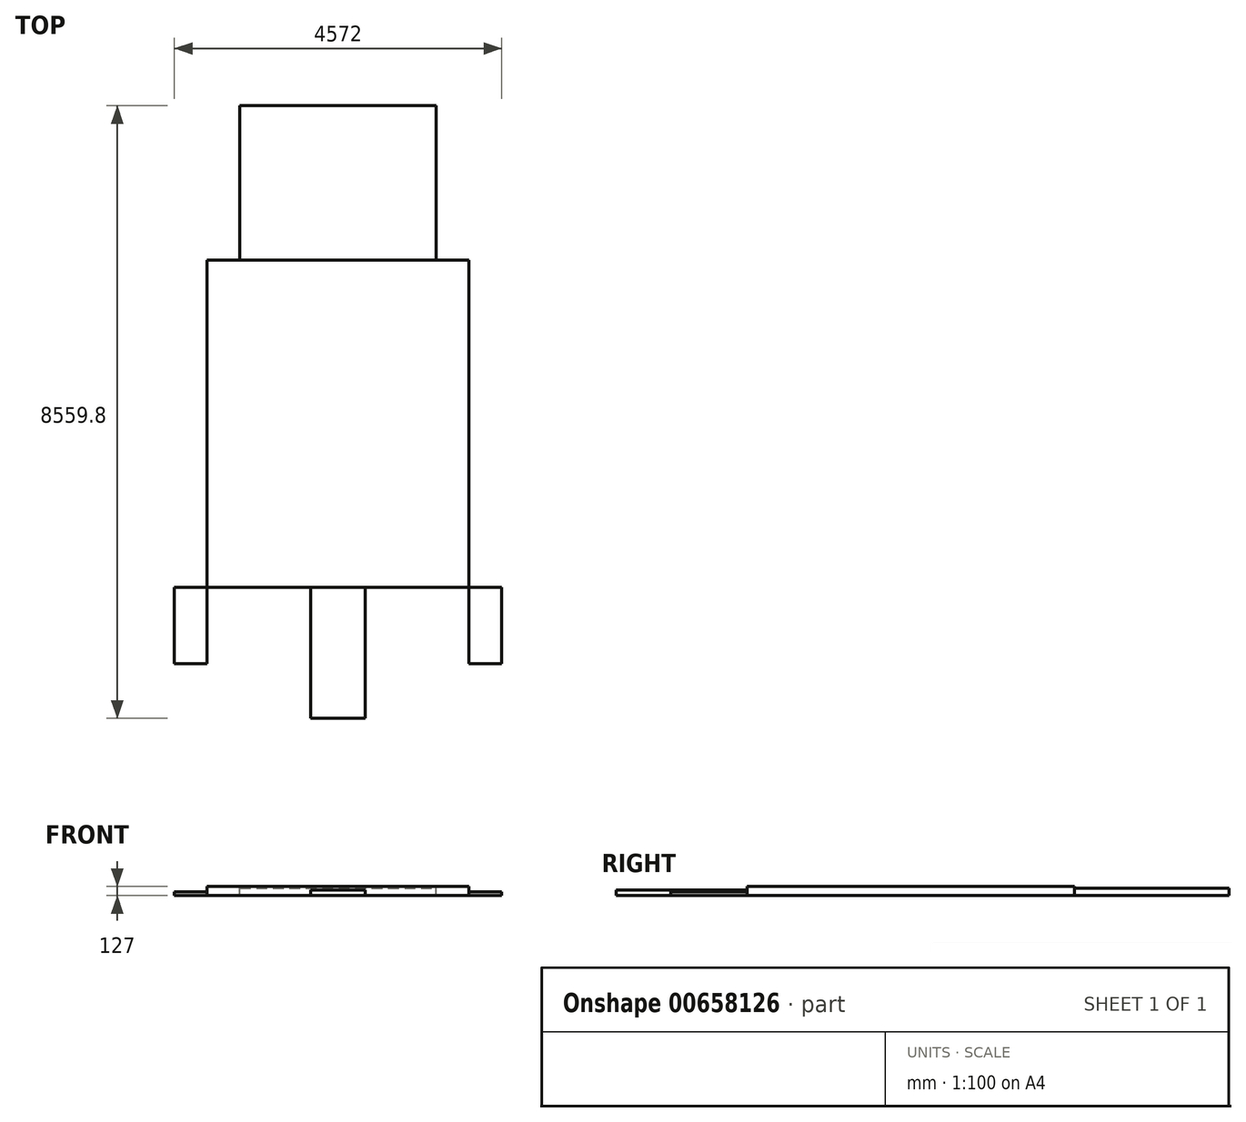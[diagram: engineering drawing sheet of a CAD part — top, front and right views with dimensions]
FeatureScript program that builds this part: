
annotation { "Feature Type Name" : "Feature", "Feature Type Description" : "" }
export const myFeature = defineFeature(function(context is Context, id is Id, definition is map)
    precondition{}
    {
        {
            var Q0;
            Q0=qCreatedBy(makeId("Top.planeOp"),FACE);
            var sketch = newSketch(context, id + "F0", { "sketchPlane" : qUnion([Q0])});
            skLineSegment(sketch, "E0.top", {"start": v(0, 4572) * mm, "end": v(3657.6, 4572) * mm});
            skLineSegment(sketch, "E0.left", {"start": v(0, 0) * mm, "end": v(0, 4572) * mm});
            skLineSegment(sketch, "E0.right", {"start": v(3657.6, 0) * mm, "end": v(3657.6, 4572) * mm});
            skLineSegment(sketch, "E1", {"start": v(0, 0) * mm, "end": v(3657.6, 0) * mm});
            skSolve(sketch);
        }
        {
            var Q0;
            Q0=makeQuery(id+"F0.imprint","IMPRINT",FACE,{"disambiguationData":[TD([[makeQuery(id+"F0.imprint","IMPRINT",EDGE,{"derivedFrom":sQuery(id+"F0.wireOp",EDGE,"E0.top")}),-1.0]])]});
            extrude(context, id + "F1", {"entities" : qUnion([Q0]), "depth" : 127 * mm, "offsetDistance" : 25.4 * mm});
        }
        {
            var Q0;
            Q0=makeQuery(id+"F1.opExtrude","CAP_FACE",FACE,{"disambiguationData":[OSD([sQuery(id+"F0.wireOp",EDGE,"E0.top"),sQuery(id+"F0.wireOp",EDGE,"E0.left"),sQuery(id+"F0.wireOp",EDGE,"E0.right"),sQuery(id+"F0.wireOp",EDGE,"LXmMFnv6-6ZTh-1Y7x-6pz1-AKVV39WLZzwZ.top"),sQuery(id+"F0.wireOp",EDGE,"LXmMFnv6-6ZTh-1Y7x-6pz1-AKVV39WLZzwZ.left"),sQuery(id+"F0.wireOp",EDGE,"LXmMFnv6-6ZTh-1Y7x-6pz1-AKVV39WLZzwZ.right"),sQuery(id+"F0.wireOp",EDGE,"AjboXFw6-qVSd-uYxO-6O3m-j0vQeSWzZkRw"),sQuery(id+"F0.wireOp",EDGE,"3yzYkoRJ-9kOB-nv2v-QkJK-sa2TvoayhQo0")])],"isStart":false});
            var sketch = newSketch(context, id + "F2", { "sketchPlane" : qUnion([Q0])});
            skPoint(sketch, "E2", {"position": v(457.2, 4572) * mm});
            skPoint(sketch, "E3", {"position": v(3200.4, 4572) * mm});
            skLineSegment(sketch, "E4.top", {"start": v(457.2, 6731) * mm, "end": v(3200.4, 6731) * mm});
            skLineSegment(sketch, "E4.left", {"start": v(457.2, 4572) * mm, "end": v(457.2, 6731) * mm});
            skLineSegment(sketch, "E4.right", {"start": v(3200.4, 4572) * mm, "end": v(3200.4, 6731) * mm});
            skLineSegment(sketch, "E5", {"start": v(457.2, 4572) * mm, "end": v(3200.4, 4572) * mm});
            skSolve(sketch);
        }
        {
            var Q0;
            Q0 = qSketchRegion(id + "F2", true);
            extrude(context, id + "F3", {"entities" : qUnion([Q0]), "oppositeDirection" : true, "depth" : 127 * mm, "offsetDistance" : 25.4 * mm, "hasSecondDirection" : true, "secondDirectionOppositeDirection" : true, "secondDirectionDepth" : 25.4 * mm});
        }
        {
            var Q0;
            Q0=makeQuery(id+"F1.opExtrude","CAP_FACE",FACE,{"disambiguationData":[OSD([sQuery(id+"F0.wireOp",EDGE,"E0.top"),sQuery(id+"F0.wireOp",EDGE,"E0.left"),sQuery(id+"F0.wireOp",EDGE,"E0.right"),sQuery(id+"F0.wireOp",EDGE,"E1")])],"isStart":false});
            var sketch = newSketch(context, id + "F4", { "sketchPlane" : qUnion([Q0])});
            skLineSegment(sketch, "E6.top", {"start": v(1447.8, -1828.8) * mm, "end": v(2209.8, -1828.8) * mm});
            skLineSegment(sketch, "E6.left", {"start": v(1447.8, 0) * mm, "end": v(1447.8, -1828.8) * mm});
            skLineSegment(sketch, "E6.right", {"start": v(2209.8, 0) * mm, "end": v(2209.8, -1828.8) * mm});
            skLineSegment(sketch, "E7", {"start": v(1447.8, 0) * mm, "end": v(2209.8, 0) * mm});
            skSolve(sketch);
        }
        {
            var Q0;
            Q0 = qSketchRegion(id + "F4", true);
            extrude(context, id + "F5", {"entities" : qUnion([Q0]), "oppositeDirection" : true, "depth" : 127 * mm, "offsetDistance" : 25.4 * mm, "hasSecondDirection" : true, "secondDirectionOppositeDirection" : true, "secondDirectionDepth" : 50.8 * mm});
        }
        {
            var Q0;
            Q0=makeQuery(id+"F1.opExtrude","CAP_FACE",FACE,{"disambiguationData":[OSD([sQuery(id+"F0.wireOp",EDGE,"E0.top"),sQuery(id+"F0.wireOp",EDGE,"E0.left"),sQuery(id+"F0.wireOp",EDGE,"E0.right"),sQuery(id+"F0.wireOp",EDGE,"E1")])],"isStart":false});
            var sketch = newSketch(context, id + "F6", { "sketchPlane" : qUnion([Q0])});
            skLineSegment(sketch, "E8.bottom", {"start": v(3657.6, 0) * mm, "end": v(4114.8, 0) * mm});
            skLineSegment(sketch, "E8.top", {"start": v(3657.6, -1066.8) * mm, "end": v(4114.8, -1066.8) * mm});
            skLineSegment(sketch, "E8.left", {"start": v(3657.6, 0) * mm, "end": v(3657.6, -1066.8) * mm});
            skLineSegment(sketch, "E8.right", {"start": v(4114.8, 0) * mm, "end": v(4114.8, -1066.8) * mm});
            skLineSegment(sketch, "E9.bottom", {"start": v(-457.2, 0) * mm, "end": v(0, 0) * mm});
            skLineSegment(sketch, "E9.top", {"start": v(-457.2, -1066.8) * mm, "end": v(0, -1066.8) * mm});
            skLineSegment(sketch, "E9.left", {"start": v(-457.2, 0) * mm, "end": v(-457.2, -1066.8) * mm});
            skLineSegment(sketch, "E9.right", {"start": v(0, 0) * mm, "end": v(0, -1066.8) * mm});
            skSolve(sketch);
        }
        {
            var Q0;
            Q0 = qSketchRegion(id + "F6", true);
            extrude(context, id + "F7", {"entities" : qUnion([Q0]), "oppositeDirection" : true, "depth" : 127 * mm, "offsetDistance" : 25.4 * mm, "hasSecondDirection" : true, "secondDirectionOppositeDirection" : true, "secondDirectionDepth" : 76.2 * mm});
        }
    });
